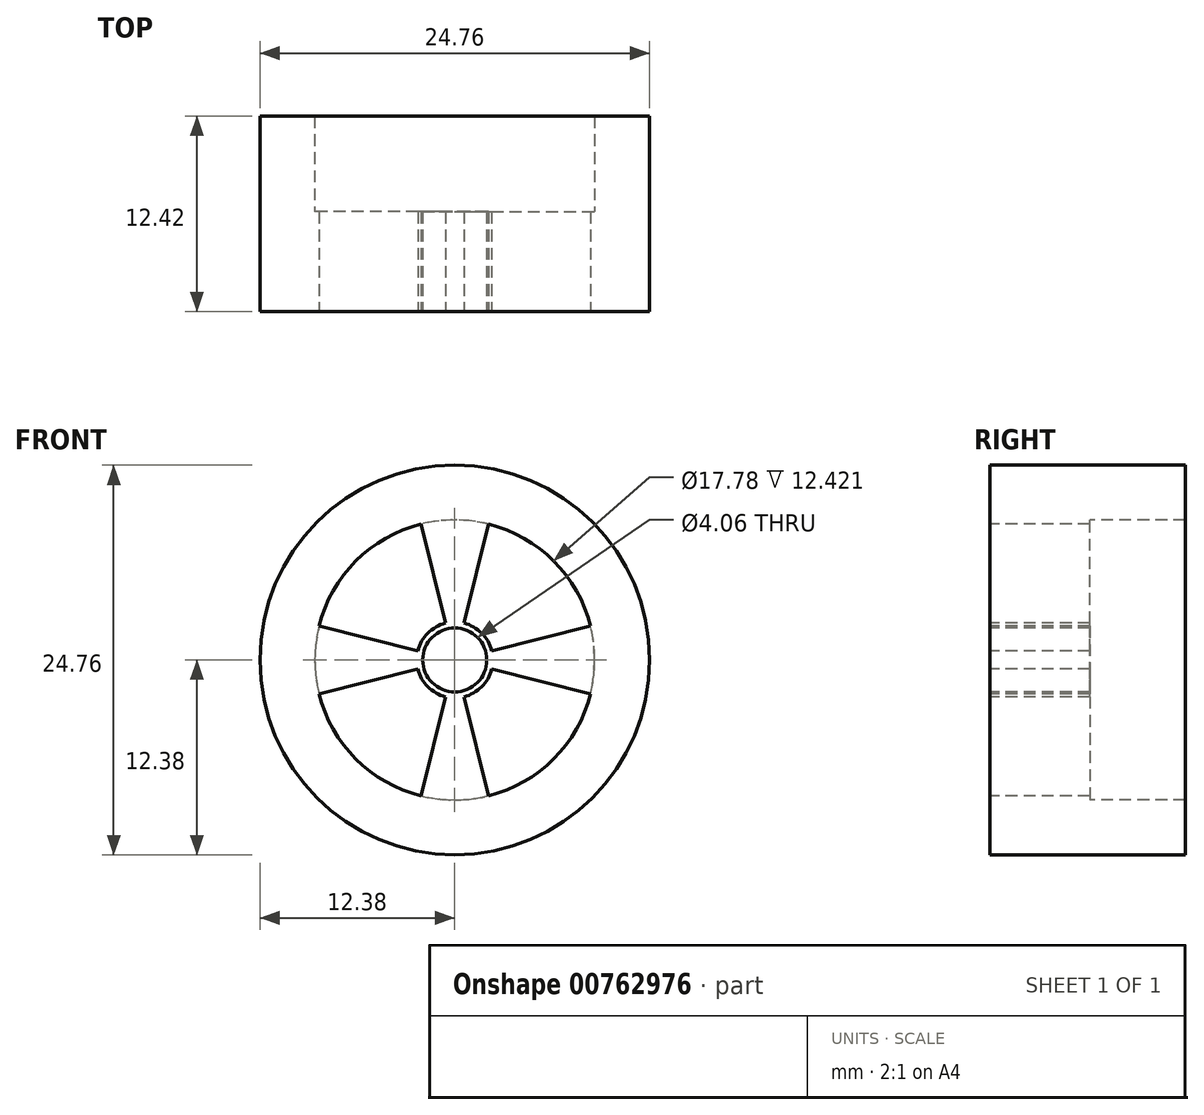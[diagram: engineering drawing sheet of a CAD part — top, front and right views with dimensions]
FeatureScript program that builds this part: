
annotation { "Feature Type Name" : "Feature", "Feature Type Description" : "" }
export const myFeature = defineFeature(function(context is Context, id is Id, definition is map)
    precondition{}
    {
        {
            var Q0;
            Q0=qCreatedBy(makeId("Right.planeOp"),FACE);
            var sketch = newSketch(context, id + "F0", { "sketchPlane" : qUnion([Q0])});
            skLineSegment(sketch, "E0.left", {"start": v(-29.24, 22.22) * mm, "end": v(-29.24, 20.32) * mm});
            skLineSegment(sketch, "E1", {"start": v(-29.24, 11.43) * mm, "end": v(-16.19, 11.43) * mm, "construction": true});
            skLineSegment(sketch, "E2.0", {"start": v(-29.24, 20.32) * mm, "end": v(-16.82, 20.32) * mm});
            skLineSegment(sketch, "E3.0", {"start": v(-16.82, 22.22) * mm, "end": v(-16.82, 20.32) * mm});
            skLineSegment(sketch, "E4.0", {"start": v(-29.24, 23.8) * mm, "end": v(-16.82, 23.8) * mm});
            skLineSegment(sketch, "E5", {"start": v(-29.24, 22.22) * mm, "end": v(-29.24, 23.8) * mm});
            skLineSegment(sketch, "E6", {"start": v(-16.82, 22.22) * mm, "end": v(-16.82, 23.8) * mm});
            skSolve(sketch);
        }
        {
            var Q0;
            Q0 = qSketchRegion(id + "F0", true);
            var Q1;
            Q1=sQuery(id+"F0.wireOp",EDGE,"E1");
            revolve(context, id + "F1", {"surfaceOperationType" : NewSurfaceOperationType.NEW, "entities" : qUnion([Q0]), "axis" : qUnion([Q1]), "revolveType" : RevolveType.FULL});
        }
        {
            var Q0;
            Q0=makeQuery(id+"F1.opRevolve","SWEPT_FACE",FACE,{"disambiguationData":[OSD([sQuery(id+"F0.wireOp",EDGE,"E0.left")])]});
            var sketch = newSketch(context, id + "F2", { "sketchPlane" : qUnion([Q0])});
            skCircle(sketch, "E7", {"center": v(0, 11.43) * mm, "radius": 2.03 * mm});
            skLineSegment(sketch, "E8", {"start": v(0, 13.67) * mm, "end": v(0, 20.32) * mm, "construction": true});
            skLineSegment(sketch, "E9", {"start": v(0, 9.4) * mm, "end": v(0, 2.54) * mm, "construction": true});
            skLineSegment(sketch, "E10", {"start": v(2.03, 11.44) * mm, "end": v(8.89, 11.44) * mm, "construction": true});
            skLineSegment(sketch, "E11", {"start": v(-2.03, 11.48) * mm, "end": v(-8.89, 11.48) * mm, "construction": true});
            skLineSegment(sketch, "E12", {"start": v(-0.58, 13.77) * mm, "end": v(-2.15, 20.06) * mm});
            skLineSegment(sketch, "E13", {"start": v(0.58, 13.77) * mm, "end": v(2.15, 20.06) * mm});
            skLineSegment(sketch, "E14", {"start": v(2.34, 12.01) * mm, "end": v(8.63, 13.58) * mm});
            skLineSegment(sketch, "E15", {"start": v(2.34, 10.85) * mm, "end": v(8.63, 9.28) * mm});
            skLineSegment(sketch, "E16", {"start": v(-0.58, 9.09) * mm, "end": v(-2.15, 2.8) * mm});
            skLineSegment(sketch, "E17", {"start": v(0.58, 9.09) * mm, "end": v(2.15, 2.8) * mm});
            skLineSegment(sketch, "E18", {"start": v(-2.34, 12.01) * mm, "end": v(-8.63, 13.58) * mm});
            skLineSegment(sketch, "E19", {"start": v(-2.34, 10.85) * mm, "end": v(-8.63, 9.28) * mm});
            skCircle(sketch, "E20.0", {"center": v(0, 11.43) * mm, "radius": 2.41 * mm});
            skCircle(sketch, "E21", {"center": v(0, 11.43) * mm, "radius": 8.9 * mm});
            skSolve(sketch);
        }
        {
            var Q0;
            {var subQ0=sQuery(id+"F2.wireOp",EDGE,"E16");Q0=makeQuery(id+"F2.imprint","IMPRINT",FACE,{"disambiguationData":[TD([[makeQuery(id+"F2.imprint","IMPRINT",EDGE,{"derivedFrom":subQ0}),1.0]])]});}
            var Q1;
            {var subQ0=sQuery(id+"F2.wireOp",EDGE,"E18");Q1=makeQuery(id+"F2.imprint","IMPRINT",FACE,{"disambiguationData":[TD([[makeQuery(id+"F2.imprint","IMPRINT",EDGE,{"derivedFrom":subQ0}),1.0]])]});}
            var Q2;
            {var subQ0=sQuery(id+"F2.wireOp",EDGE,"E12");Q2=makeQuery(id+"F2.imprint","IMPRINT",FACE,{"disambiguationData":[TD([[makeQuery(id+"F2.imprint","IMPRINT",EDGE,{"derivedFrom":subQ0}),-1.0]])]});}
            var Q3;
            {var subQ0=sQuery(id+"F2.wireOp",EDGE,"E14");Q3=makeQuery(id+"F2.imprint","IMPRINT",FACE,{"disambiguationData":[TD([[makeQuery(id+"F2.imprint","IMPRINT",EDGE,{"derivedFrom":subQ0}),-1.0]])]});}
            var Q4;
            Q4=makeQuery(id+"F2.imprint","IMPRINT",FACE,{"disambiguationData":[TD([[makeQuery(id+"F2.imprint","IMPRINT",EDGE,{"derivedFrom":sQuery(id+"F2.wireOp",EDGE,"E7")}),-1.0]])]});
            extrude(context, id + "F3", {"entities" : qUnion([Q0, Q1, Q2, Q3, Q4]), "operationType" : NewBodyOperationType.ADD, "oppositeDirection" : true, "depth" : 6.35 * mm, "offsetDistance" : 25.4 * mm});
        }
    });
